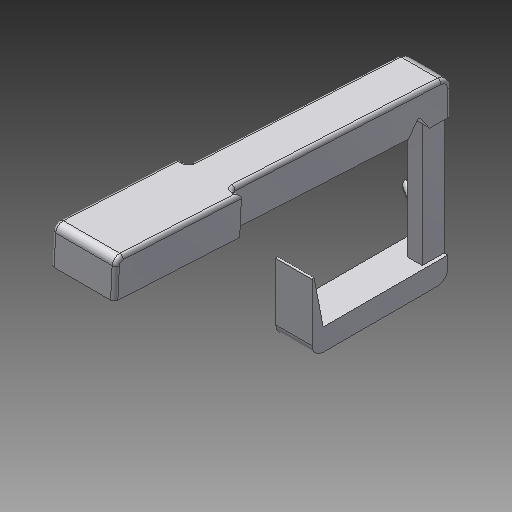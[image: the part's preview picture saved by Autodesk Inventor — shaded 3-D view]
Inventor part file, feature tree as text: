
AUTODESK INVENTOR PART (.ipt)
format: ipt  version: 2018 (Build 220112000, 112)  size: 307,712 bytes
history: native  units: mm
features: extrude x7, fillet x6, other x3, draft x1, chamfer x1
ambient origin geometry x8: Origin, YZ Plane, XZ Plane, XY Plane, X Axis, Y Axis, Z Axis, Center Point
bodies: Solid1 (feature_tree)
feature tree (18):
  other  "Key Sketch"
  extrude  "Upper Key"  Depth=10.0mm
  extrude  "Lower Key"  Depth=1.0mm
  other  "Hinge Cut Sketch"
  extrude  "Hinge Cut"  Depth=10.0mm TaperAngle=0.0deg
  extrude  "Hinge Cut 2"  Depth=3.0mm
  other  "Lever Sketch"
  extrude  "Vertical Lever"  Depth=3.0mm
  extrude  "Horizontal Lever"  Depth=33.6625mm
  extrude  "Spring Hook"  Depth=0.5mm
  draft  "FaceDraft3"
  chamfer  "Chamfer1"  Distance=3.0mm
  fillet  "Fillet9"  Radius=6.0mm
  fillet  "Fillet10"  Radius=4.0mm
  fillet  "Fillet5"  Radius=10.0mm
  fillet  "Fillet4"  [1 undecoded]
  fillet  "Fillet11"  Radius=3.0mm
  fillet  "Fillet14"  Radius=2.3mm
note: 1 required parameter value undecoded (feature->parameter linkage not recoverable at this tier; creation-order binding heuristic only, values carry confidence <= 0.55)
